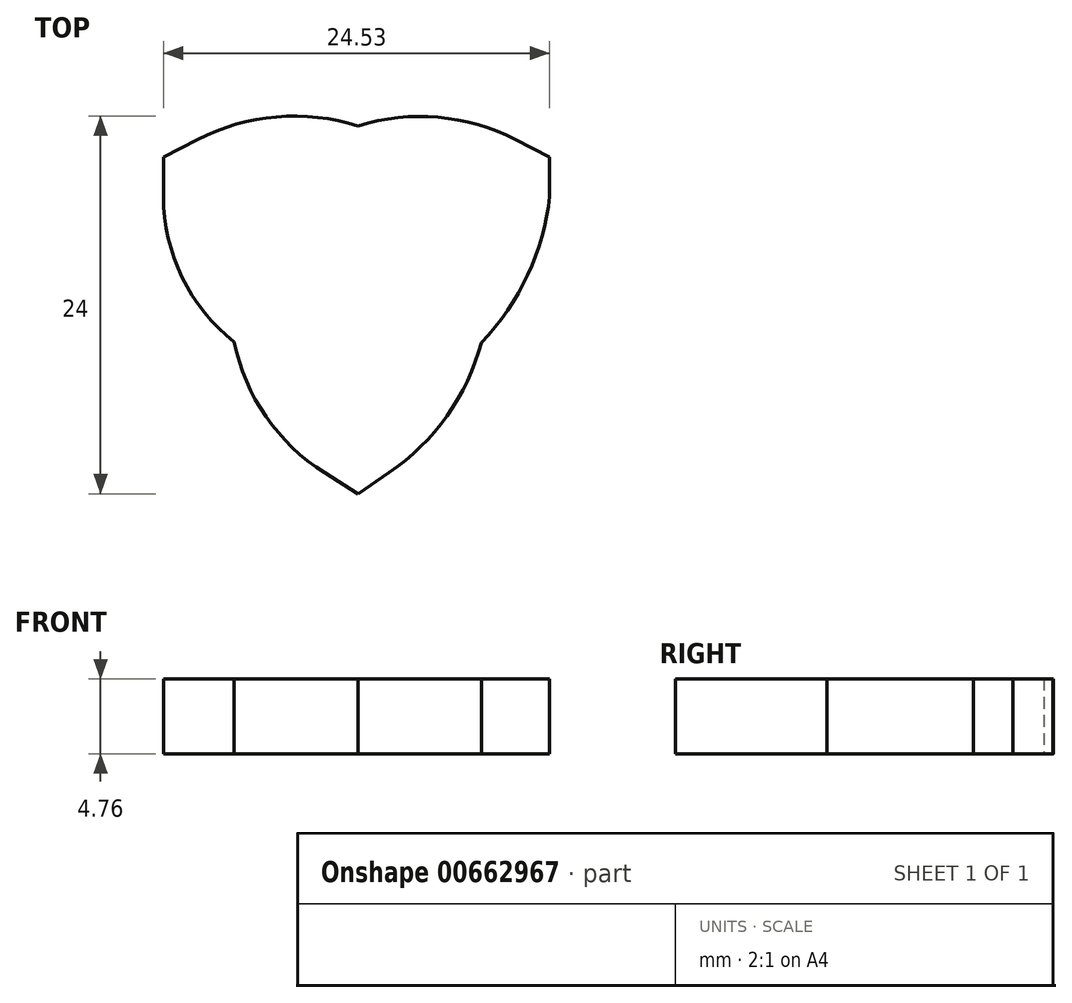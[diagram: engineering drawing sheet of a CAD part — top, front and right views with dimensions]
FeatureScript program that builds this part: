
annotation { "Feature Type Name" : "Feature", "Feature Type Description" : "" }
export const myFeature = defineFeature(function(context is Context, id is Id, definition is map)
    precondition{}
    {
        {
            var Q0;
            Q0=qCreatedBy(makeId("Top.planeOp"),FACE);
            var sketch = newSketch(context, id + "F0", { "sketchPlane" : qUnion([Q0])});
            skPoint(sketch, "E0.center", {"position": v(0, 0) * mm});
            skLineSegment(sketch, "E1", {"start": v(-10.2, 8.25) * mm, "end": v(-12.37, 7.15) * mm});
            skLineSegment(sketch, "E2", {"start": v(-12.37, 7.15) * mm, "end": v(-12.37, 4.64) * mm});
            skLineSegment(sketch, "E3.MirrorCS", {"start": v(12.16, 7.15) * mm, "end": v(12.16, 4.64) * mm});
            skLineSegment(sketch, "E4.MirrorCS", {"start": v(10, 8.25) * mm, "end": v(12.16, 7.15) * mm});
            skLineSegment(sketch, "E5", {"start": v(1.97, -12.9) * mm, "end": v(0, -14.26) * mm});
            skLineSegment(sketch, "E6", {"start": v(0, -14.26) * mm, "end": v(-2.14, -12.9) * mm});
            skLineSegment(sketch, "E7", {"start": v(-12.37, 4.64) * mm, "end": v(-12.37, 4.57) * mm});
            skArc(sketch, "E8", {"start": v(0, 9.12) * mm, "mid": v(-5.19, 9.69) * mm, "end": v(-10.2, 8.25) * mm});
            skArc(sketch, "E9", {"start": v(10, 8.25) * mm, "mid": v(5.08, 9.66) * mm, "end": v(0, 9.12) * mm});
            skArc(sketch, "E10", {"start": v(1.97, -12.9) * mm, "mid": v(5.64, -9.3) * mm, "end": v(7.82, -4.64) * mm});
            skArc(sketch, "E11", {"start": v(7.82, -4.64) * mm, "mid": v(10.76, -0.36) * mm, "end": v(12.16, 4.64) * mm});
            skArc(sketch, "E12", {"start": v(-7.87, -4.61) * mm, "mid": v(-5.86, -9.35) * mm, "end": v(-2.14, -12.9) * mm});
            skArc(sketch, "E13", {"start": v(-12.37, 4.64) * mm, "mid": v(-11.19, -0.5) * mm, "end": v(-7.87, -4.61) * mm});
            skSolve(sketch);
        }
        {
            var Q0;
            Q0=makeQuery(id+"F0.imprint","IMPRINT",FACE,{"disambiguationData":[TD([[makeQuery(id+"F0.imprint","IMPRINT",EDGE,{"derivedFrom":sQuery(id+"F0.wireOp",EDGE,"E1")}),1.0]])]});
            extrude(context, id + "F1", {"entities" : qUnion([Q0]), "depth" : 4.76 * mm, "offsetDistance" : 25.4 * mm});
        }
    });
